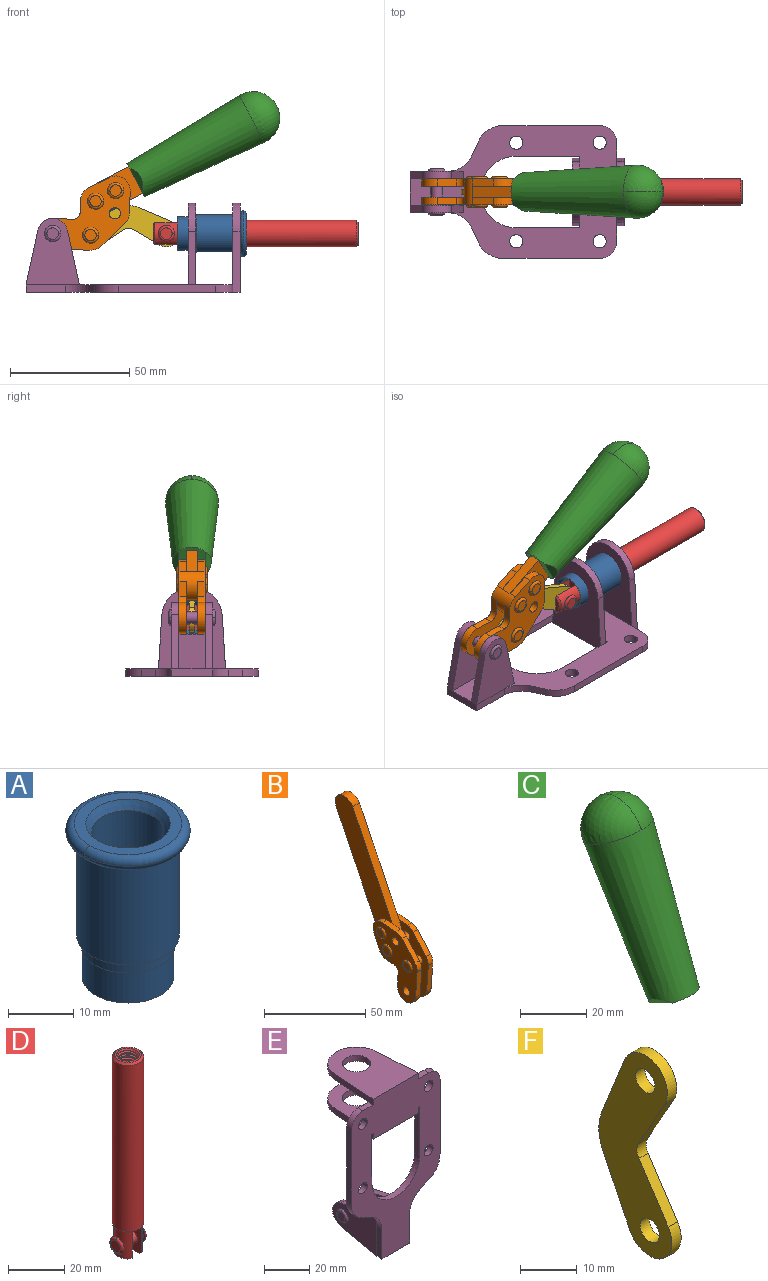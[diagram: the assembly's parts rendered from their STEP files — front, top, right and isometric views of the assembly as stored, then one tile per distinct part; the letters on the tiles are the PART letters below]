
ASSEMBLY  parts=6 mates=6
PART A: 15 faces, bbox 20.6x20.6x28.7 mm
  f0: torus R=8.26mm, axis (0,0,1), area 56.8mm2, adj f1,f10,f12
  f1: torus R=8.26mm, axis (0,0,1), area 56.8mm2, adj f0,f6,f13
  f2: cylinder r=5.59mm len=25.91mm, axis (0,0,1), area 909.6mm2, adj f3,f4
  f3: cone r=6.86mm half-angle=45deg, axis (0,0,-1), area 70.2mm2, adj f2,f14
  f4: cone r=6.47mm half-angle=30deg, axis (0,0,1), area 66.7mm2, adj f2,f13
  f5: cylinder r=7.04mm len=14.07mm, axis (0,0,1), area 252.6mm2, adj f11,f14
  f6: torus R=8.26mm, axis (0,0,1), area 56.8mm2, adj f1,f12,f13
  f7: cylinder r=7.16mm len=14.33mm, axis (0,0,1), area 91.5mm2, adj f9,f11
  f8: cylinder r=7.86mm len=18.42mm, axis (0,0,1), area 909.6mm2, adj f9,f10
  f9: plane 15.72x15.72mm, normal (0,0,-1), area 33mm2, adj f7,f8
  f10: plane 16.51x16.51mm, normal (0,0,-1), area 19.9mm2, adj f0,f8,f12
  f11: plane 14.33x14.33mm, normal (0,0,-1), area 5.7mm2, adj f5,f7
  f12: torus R=8.26mm, axis (0,0,1), area 56.8mm2, adj f0,f6,f10
  f13: plane 16.51x16.51mm, normal (0,0,1), area 82.7mm2, adj f1,f4,f6
  f14: plane 14.07x14.07mm, normal (0,0,-1), area 7.8mm2, adj f3,f5
PART B: 59 faces, bbox 12.9x60.2x99.6 mm
  f0: torus R=2.39mm, axis (-1,0,0), area 14.9mm2, adj f20,f43,f51
  f1: torus R=2.39mm, axis (-1,0,0), area 14.9mm2, adj f19,f42,f51
  f2: torus R=2.39mm, axis (-1,0,0), area 14.9mm2, adj f18,f35,f51
  f3: torus R=2.39mm, axis (-1,0,0), area 14.9mm2, adj f14,f17,f23
  f4: torus R=2.39mm, axis (-1,0,0), area 14.9mm2, adj f13,f16,f23
  f5: torus R=2.39mm, axis (-1,0,0), area 14.9mm2, adj f12,f15,f23
  f6: cylinder r=2.39mm len=4.78mm, axis (1,0,0), area 46.5mm2, adj f48,f50,f51
  f7: cylinder r=2.39mm len=4.78mm, axis (1,0,0), area 46.5mm2, adj f50,f51
  f8: cylinder r=6.35mm len=12.68mm, axis (1,0,0), area 61.8mm2, adj f38,f39,f50,f51
  f9: cylinder r=2.39mm len=4.78mm, axis (-1,0,0), area 70.5mm2, adj f46,f50
  f10: cylinder r=2.39mm len=4.78mm, axis (-1,0,0), area 46.5mm2, adj f23,f45,f46
  f11: cylinder r=2.39mm len=4.78mm, axis (-1,0,0), area 46.5mm2, adj f23,f46
  f12: plane 4.78x4.78mm, normal (1,0,0), area 17.9mm2, adj f5,f15
  f13: plane 4.78x4.78mm, normal (1,0,0), area 17.9mm2, adj f4,f16
  f14: plane 4.78x4.78mm, normal (1,0,0), area 17.9mm2, adj f3,f17
  f15: torus R=2.39mm, axis (-1,0,0), area 14.9mm2, adj f5,f12,f23
  f16: torus R=2.39mm, axis (-1,0,0), area 14.9mm2, adj f4,f13,f23
  f17: torus R=2.39mm, axis (-1,0,0), area 14.9mm2, adj f3,f14,f23
  f18: plane 4.78x4.78mm, normal (-1,0,0), area 17.9mm2, adj f2,f35
  f19: plane 4.78x4.78mm, normal (-1,0,0), area 17.9mm2, adj f1,f42
  f20: plane 4.78x4.78mm, normal (-1,0,0), area 17.9mm2, adj f0,f43
  f21: plane 2.26x0.2mm, normal (1,0,0), area 0.2mm2, adj f31,f44
  f22: plane 2.26x0.2mm, normal (-1,0,0), area 0.2mm2, adj f41,f44
  f23: plane 39.37x30.77mm, normal (1,0,0), area 565.5mm2, adj f3,f4,f5,f10,f11,f15,f16,f17
  f24: cylinder r=6.1mm len=4.15mm, axis (-1,0,0), area 14.7mm2, adj f23,f25,f32,f46
  f25: plane 10.25x9.01mm, normal (0,-0.75,0.66), area 42.3mm2, adj f23,f24,f26,f46
  f26: cylinder r=6.35mm len=4.64mm, axis (-1,0,0), area 15.6mm2, adj f23,f25,f27,f46
  f27: plane 15.84x3.1mm, normal (0,-1,-0.07), area 49.2mm2, adj f23,f26,f28,f46
  f28: cylinder r=6.35mm len=12.68mm, axis (-1,0,0), area 61.8mm2, adj f23,f27,f29,f46
  f29: plane 8.11x3.1mm, normal (0,1,0.07), area 25.2mm2, adj f23,f28,f30,f46
  f30: cylinder r=3.05mm len=3.25mm, axis (-1,0,0), area 14.8mm2, adj f23,f29,f31,f46
  f31: plane 5.99x3.1mm, normal (0,0.07,-1), area 18.6mm2, adj f21,f23,f30,f44,f46
  f32: plane 9.5x3.1mm, normal (0,-0.07,1), area 29.5mm2, adj f23,f24,f33,f46,f47
  f33: cylinder r=6.1mm len=8.63mm, axis (-1,0,0), area 39.1mm2, adj f23,f32,f34,f47
  f34: plane 8.65x3.96mm, normal (0,0.91,-0.42), area 29.5mm2, adj f23,f33,f44,f47
  f35: torus R=2.39mm, axis (-1,0,0), area 14.9mm2, adj f2,f18,f51
  f36: plane 10.25x9.01mm, normal (0,-0.75,0.66), area 42.3mm2, adj f37,f49,f50,f51
  f37: cylinder r=6.35mm len=4.64mm, axis (1,0,0), area 15.6mm2, adj f36,f38,f50,f51
  f38: plane 15.84x3.1mm, normal (0,-1,-0.07), area 49.2mm2, adj f8,f37,f50,f51
  f39: plane 8.11x3.1mm, normal (0,1,0.07), area 25.2mm2, adj f8,f40,f50,f51
  f40: cylinder r=3.05mm len=3.25mm, axis (1,0,0), area 14.8mm2, adj f39,f41,f50,f51
  f41: plane 5.99x3.1mm, normal (0,0.07,-1), area 18.6mm2, adj f22,f40,f44,f50,f51
  f42: torus R=2.39mm, axis (-1,0,0), area 14.9mm2, adj f1,f19,f51
  f43: torus R=2.39mm, axis (-1,0,0), area 14.9mm2, adj f0,f20,f51
  f44: cylinder r=6.35mm len=12.12mm, axis (-1,0,0), area 128.9mm2, adj f21,f22,f23,f31,f34,f41,f46,f47
  f45: plane 2.65x1.35mm, normal (1,0,0), area 1mm2, adj f10,f55
  f46: plane 39.08x20.42mm, normal (-1,0,0), area 412.5mm2, adj f9,f10,f11,f24,f25,f26,f27,f28
  f47: plane 77.62x39.82mm, normal (1,0,0), area 850mm2, adj f32,f33,f34,f44,f53,f54,f55
  f48: plane 2.65x1.35mm, normal (-1,0,0), area 1mm2, adj f6,f55
  f49: cylinder r=6.1mm len=4.15mm, axis (1,0,0), area 14.7mm2, adj f36,f50,f51,f56
  f50: plane 39.08x20.42mm, normal (1,0,0), area 412.5mm2, adj f6,f7,f8,f9,f36,f37,f38,f39
  f51: plane 39.37x30.77mm, normal (-1,0,0), area 565.5mm2, adj f0,f1,f2,f6,f7,f8,f35,f36
  f52: plane 8.65x3.96mm, normal (0,0.91,-0.42), area 29.5mm2, adj f44,f51,f57,f58
  f53: plane 68.49x33.4mm, normal (0,0.9,-0.44), area 358.1mm2, adj f44,f47,f54,f58
  f54: cylinder r=6.35mm len=12.06mm, axis (1,0,0), area 93.7mm2, adj f47,f53,f55,f58
  f55: plane 68.49x33.4mm, normal (0,-0.9,0.44), area 358.1mm2, adj f44,f45,f46,f47,f48,f50,f54,f58
  f56: plane 9.5x3.1mm, normal (0,-0.07,1), area 29.5mm2, adj f49,f50,f51,f57,f58
  f57: cylinder r=6.1mm len=8.63mm, axis (1,0,0), area 39.1mm2, adj f51,f52,f56,f58
  f58: plane 77.62x39.82mm, normal (-1,0,0), area 850mm2, adj f44,f52,f53,f54,f55,f56,f57
PART C: 11 faces, bbox 22.3x42.6x64.5 mm
  f0: sphere r=11.13mm, area 411.4mm2, adj f1,f8
  f1: cone r=11.11mm half-angle=3.3deg, axis (0,0.44,0.9), area 3251.8mm2, adj f0,f7,f8,f9,f10
  f2: cylinder r=6.16mm len=11.7mm, axis (1,0,0), area 89.5mm2, adj f3,f4,f5,f6
  f3: plane 60.23x36.75mm, normal (-1,0,0), area 763.6mm2, adj f2,f4,f6,f10
  f4: plane 51.37x25.05mm, normal (0,0.9,-0.44), area 264.2mm2, adj f2,f3,f5,f10
  f5: plane 60.23x36.75mm, normal (1,0,0), area 763.6mm2, adj f2,f4,f6,f10
  f6: plane 51.37x25.05mm, normal (0,-0.9,0.44), area 264.2mm2, adj f2,f3,f5,f10
  f7: plane 9.95x5.95mm, normal (0.71,-0.31,-0.64), area 25.8mm2, adj f1,f10
  f8: sphere r=11.13mm, area 411.4mm2, adj f0,f1
  f9: plane 9.95x5.95mm, normal (-0.71,-0.31,-0.64), area 25.8mm2, adj f1,f10
  f10: plane 14.27x11.38mm, normal (0,-0.44,-0.9), area 106.7mm2, adj f1,f3,f4,f5,f6,f7,f9
PART D: 48 faces, bbox 12.6x11.1x86.1 mm
  f0: torus R=2.41mm, axis (-1,0,0), area 15mm2, adj f30,f32,f34
  f1: torus R=2.41mm, axis (-1,0,0), area 15mm2, adj f29,f31,f33
  f2: cylinder r=5.54mm len=72.39mm, axis (0,0,1), area 2518.5mm2, adj f3,f4,f42,f43
  f3: cone r=5.54mm half-angle=45deg, axis (0,0,1), area 7.6mm2, adj f2,f5,f41
  f4: cone r=5.54mm half-angle=45deg, axis (0,0,-1), area 34.9mm2, adj f2,f39
  f5: cylinder r=5.08mm len=11.48mm, axis (0,0,1), area 108.3mm2, adj f3,f7,f8,f41
  f6: cylinder r=2.41mm len=4.83mm, axis (-1,0,0), area 71.2mm2, adj f40,f41
  f7: cylinder r=2.41mm len=4.83mm, axis (-1,0,0), area 7.6mm2, adj f5,f34
  f8: cone r=5.08mm half-angle=45deg, axis (0,0,1), area 10.6mm2, adj f5,f37,f41
  f9: cone r=3.98mm half-angle=45deg, axis (0,0,1), area 17.6mm2, adj f27,f39,f45,f46,f47
  f10: cylinder r=2.41mm len=4.83mm, axis (-1,0,0), area 7.6mm2, adj f33,f38
  f11: cylinder r=3.2mm len=6.4mm, axis (0,0,1), area 78.4mm2, adj f12,f28,f44,f45,f47
  f12: cylinder r=3.2mm len=6.4mm, axis (0,0,1), area 10.5mm2, adj f11,f13,f45,f47
  f13: cylinder r=3.2mm len=6.4mm, axis (0,0,1), area 10.5mm2, adj f12,f14,f45,f47
  f14: cylinder r=3.2mm len=6.4mm, axis (0,0,1), area 10.5mm2, adj f13,f15,f45,f47
  f15: cylinder r=3.2mm len=6.4mm, axis (0,0,1), area 10.5mm2, adj f14,f16,f45,f47
  f16: cylinder r=3.2mm len=6.4mm, axis (0,0,1), area 10.5mm2, adj f15,f17,f45,f47
  f17: cylinder r=3.2mm len=6.4mm, axis (0,0,1), area 10.5mm2, adj f16,f18,f45,f47
  f18: cylinder r=3.2mm len=6.4mm, axis (0,0,1), area 10.5mm2, adj f17,f19,f45,f47
  f19: cylinder r=3.2mm len=6.4mm, axis (0,0,1), area 10.5mm2, adj f18,f20,f45,f47
  f20: cylinder r=3.2mm len=6.4mm, axis (0,0,1), area 10.5mm2, adj f19,f21,f45,f47
  f21: cylinder r=3.2mm len=6.4mm, axis (0,0,1), area 10.5mm2, adj f20,f22,f45,f47
  f22: cylinder r=3.2mm len=6.4mm, axis (0,0,1), area 10.5mm2, adj f21,f23,f45,f47
  f23: cylinder r=3.2mm len=6.4mm, axis (0,0,1), area 10.5mm2, adj f22,f24,f45,f47
  f24: cylinder r=3.2mm len=6.4mm, axis (0,0,1), area 10.5mm2, adj f23,f25,f45,f47
  f25: cylinder r=3.2mm len=6.4mm, axis (0,0,1), area 10.5mm2, adj f24,f26,f45,f47
  f26: cylinder r=3.2mm len=6.4mm, axis (0,0,1), area 10.5mm2, adj f25,f27,f45,f47
  f27: cylinder r=3.2mm len=6.4mm, axis (0,0,1), area 7.4mm2, adj f9,f26,f45,f47
  f28: cone r=3.2mm half-angle=60deg, axis (0,0,1), area 37.2mm2, adj f11
  f29: plane 4.83x4.83mm, normal (-1,0,0), area 18.3mm2, adj f1,f31
  f30: plane 4.83x4.83mm, normal (1,0,0), area 18.3mm2, adj f0,f32
  f31: torus R=2.41mm, axis (-1,0,0), area 15mm2, adj f1,f29,f33
  f32: torus R=2.41mm, axis (-1,0,0), area 15mm2, adj f0,f30,f34
  f33: plane 6.83x6.83mm, normal (1,0,0), area 18.3mm2, adj f1,f10,f31
  f34: plane 6.83x6.83mm, normal (-1,0,0), area 18.3mm2, adj f0,f7,f32
  f35: cone r=5.08mm half-angle=45deg, axis (0,0,1), area 10.6mm2, adj f36,f38,f40
  f36: plane 7.25x1.97mm, normal (0,0,-1), area 10mm2, adj f35,f40
  f37: plane 7.25x1.97mm, normal (0,0,-1), area 10mm2, adj f8,f41
  f38: cylinder r=5.08mm len=11.48mm, axis (0,0,1), area 108.3mm2, adj f10,f35,f40,f42
  f39: plane 9.55x9.55mm, normal (0,0,1), area 22mm2, adj f4,f9
  f40: plane 12.76x10.09mm, normal (1,0,0), area 95.7mm2, adj f6,f35,f36,f38,f42,f43
  f41: plane 12.76x10.09mm, normal (-1,0,0), area 95.7mm2, adj f3,f5,f6,f8,f37,f43
  f42: cone r=5.54mm half-angle=45deg, axis (0,0,1), area 7.6mm2, adj f2,f38,f40
  f43: plane 11.07x4.7mm, normal (0,0,-1), area 50.4mm2, adj f2,f40,f41
  f44: plane 0.89x0.62mm, normal (-1,0,0), area 0.3mm2, adj f11,f45,f46,f47
  f45: bspline ~24.8x7.63mm, area 266.6mm2, adj f9,f11,f12,f13,f14,f15,f16,f17
  f46: bspline ~24.87x7.63mm, area 73.6mm2, adj f9,f44,f45,f47
  f47: bspline ~24.98x7.63mm, area 272.5mm2, adj f9,f11,f12,f13,f14,f15,f16,f17
PART E: 55 faces, bbox 55.7x37.4x89.8 mm
  f0: torus R=2.41mm, axis (-1,0,0), area 15mm2, adj f11,f15,f25
  f1: torus R=2.41mm, axis (-1,0,0), area 15mm2, adj f10,f12,f22
  f2: cylinder r=2.78mm len=5.56mm, axis (0,-1,0), area 54.2mm2, adj f30,f54
  f3: cylinder r=14.99mm len=29.97mm, axis (0,-1,0), area 145.9mm2, adj f30,f49,f53,f54
  f4: cylinder r=2.78mm len=5.56mm, axis (0,-1,0), area 54.2mm2, adj f30,f54
  f5: cylinder r=2.78mm len=5.56mm, axis (0,-1,0), area 54.2mm2, adj f30,f54
  f6: cylinder r=2.78mm len=5.56mm, axis (0,-1,0), area 54.2mm2, adj f30,f54
  f7: cylinder r=6.35mm len=12.7mm, axis (0,0,1), area 123.6mm2, adj f27,f51
  f8: cylinder r=6.35mm len=12.7mm, axis (0,0,-1), area 124.7mm2, adj f21,f35
  f9: cylinder r=2.41mm len=11.18mm, axis (-1,0,0), area 169.4mm2, adj f16,f19
  f10: plane 4.83x4.83mm, normal (1,0,0), area 18.3mm2, adj f1,f12
  f11: plane 4.83x4.83mm, normal (-1,0,0), area 18.3mm2, adj f0,f15
  f12: torus R=2.41mm, axis (-1,0,0), area 15mm2, adj f1,f10,f22
  f13: cylinder r=6.35mm len=12.41mm, axis (1,0,0), area 53.4mm2, adj f18,f19,f22,f23
  f14: cylinder r=6.35mm len=12.41mm, axis (-1,0,0), area 53.4mm2, adj f16,f17,f24,f25
  f15: torus R=2.41mm, axis (-1,0,0), area 15mm2, adj f0,f11,f25
  f16: plane 27.86x22.35mm, normal (1,0,0), area 425.4mm2, adj f9,f14,f17,f24,f30
  f17: plane 22.86x4.97mm, normal (0,0.21,0.98), area 72.5mm2, adj f14,f16,f25,f30
  f18: plane 22.86x4.97mm, normal (0,0.21,0.98), area 72.5mm2, adj f13,f19,f22,f30
  f19: plane 27.86x22.35mm, normal (-1,0,0), area 425.4mm2, adj f9,f13,f18,f23,f30
  f20: cylinder r=12.7mm len=25.35mm, axis (0,0,-1), area 119.8mm2, adj f21,f34,f35,f36
  f21: plane 34.21x28.07mm, normal (0,0,-1), area 702.4mm2, adj f8,f20,f30,f34,f36
  f22: plane 27.96x22.45mm, normal (1,0,0), area 407.2mm2, adj f1,f12,f13,f18,f23,f30,f42,f43
  f23: plane 22.86x4.97mm, normal (0,0.21,-0.98), area 72.5mm2, adj f13,f19,f22,f44
  f24: plane 22.86x4.97mm, normal (0,0.21,-0.98), area 72.5mm2, adj f14,f16,f25,f44
  f25: plane 27.86x22.35mm, normal (-1,0,0), area 407.1mm2, adj f0,f14,f15,f17,f24,f30,f45,f46
  f26: plane 3.1x0.95mm, normal (0,0,-1), area 2.7mm2, adj f30,f49,f50,f54
  f27: plane 34.21x28.07mm, normal (0,0,1), area 702.4mm2, adj f7,f28,f30,f50,f52
  f28: cylinder r=12.7mm len=25.35mm, axis (0,0,1), area 118.8mm2, adj f27,f50,f51,f52
  f29: plane 3.1x0.95mm, normal (0,0,-1), area 2.7mm2, adj f30,f52,f53,f54
  f30: plane 86.54x55.63mm, normal (0,1,0), area 2362.9mm2, adj f2,f3,f4,f5,f6,f16,f17,f18
  f31: plane 40.56x3.1mm, normal (-1,0,0), area 125.7mm2, adj f30,f32,f48,f54
  f32: cylinder r=7.11mm len=7.11mm, axis (0,-1,0), area 34.6mm2, adj f30,f31,f33,f54
  f33: plane 6.67x3.1mm, normal (0,0,1), area 20.4mm2, adj f30,f32,f34,f54
  f34: plane 25.39x3.13mm, normal (-1,0.06,0), area 79.5mm2, adj f20,f21,f33,f35,f54
  f35: plane 37.31x28.45mm, normal (0,0,1), area 789.9mm2, adj f8,f20,f34,f36,f54
  f36: plane 25.39x3.13mm, normal (1,0.06,0), area 79.5mm2, adj f20,f21,f35,f37,f54
  f37: plane 6.67x3.1mm, normal (0,0,1), area 20.4mm2, adj f30,f36,f38,f54
  f38: cylinder r=7.11mm len=7.11mm, axis (0,-1,0), area 34.6mm2, adj f30,f37,f39,f54
  f39: plane 40.56x3.1mm, normal (1,0,0), area 125.7mm2, adj f30,f38,f40,f54
  f40: cylinder r=11.18mm len=10.16mm, axis (0,-1,0), area 39.5mm2, adj f30,f39,f41,f54
  f41: plane 6.09x3.1mm, normal (0.42,0,-0.91), area 20.8mm2, adj f30,f40,f42,f54
  f42: cylinder r=11.18mm len=9.41mm, axis (0,-1,0), area 37.2mm2, adj f22,f30,f41,f43,f54
  f43: plane 16.5x3.1mm, normal (1,0,0), area 51.1mm2, adj f22,f42,f44,f54
  f44: plane 17.37x3.1mm, normal (0,0,-1), area 53.8mm2, adj f23,f24,f30,f43,f45,f54
  f45: plane 16.5x3.1mm, normal (-1,0,0), area 51.1mm2, adj f25,f44,f46,f54
  f46: cylinder r=11.18mm len=9.41mm, axis (0,-1,0), area 37.2mm2, adj f25,f30,f45,f47,f54
  f47: plane 6.09x3.1mm, normal (-0.42,0,-0.91), area 20.8mm2, adj f30,f46,f48,f54
  f48: cylinder r=11.18mm len=10.16mm, axis (0,-1,0), area 39.5mm2, adj f30,f31,f47,f54
  f49: plane 26.54x3.1mm, normal (-1,0,0), area 82.3mm2, adj f3,f26,f30,f54
  f50: plane 25.39x3.1mm, normal (1,0.06,0), area 78.8mm2, adj f26,f27,f28,f51,f54
  f51: plane 37.31x28.45mm, normal (0,0,-1), area 789.9mm2, adj f7,f28,f50,f52,f54
  f52: plane 25.39x3.1mm, normal (-1,0.06,0), area 78.8mm2, adj f27,f28,f29,f51,f54
  f53: plane 26.54x3.1mm, normal (1,0,0), area 82.3mm2, adj f3,f29,f30,f54
  f54: plane 89.66x55.63mm, normal (0,-1,0), area 2678.5mm2, adj f2,f3,f4,f5,f6,f26,f29,f31
PART F: 12 faces, bbox 2.3x18.2x42.8 mm
  f0: cylinder r=2.4mm len=4.8mm, axis (1,0,0), area 34.9mm2, adj f4,f11
  f1: cylinder r=10.41mm len=8.47mm, axis (1,0,0), area 20.2mm2, adj f4,f9,f10,f11
  f2: cylinder r=3.05mm len=3.16mm, axis (1,0,0), area 7.7mm2, adj f4,f6,f7,f11
  f3: cylinder r=2.4mm len=4.8mm, axis (1,0,0), area 34.9mm2, adj f4,f11
  f4: plane 42.81x18.23mm, normal (-1,0,0), area 414.1mm2, adj f0,f1,f2,f3,f5,f6,f7,f8
  f5: cylinder r=5.54mm len=10.67mm, axis (1,0,0), area 41.8mm2, adj f4,f6,f10,f11
  f6: plane 11.66x6.53mm, normal (0,-0.87,-0.49), area 30.9mm2, adj f2,f4,f5,f11
  f7: plane 11.17x7.33mm, normal (0,-0.84,0.55), area 30.9mm2, adj f2,f4,f8,f11
  f8: cylinder r=5.54mm len=10.51mm, axis (1,0,0), area 41.8mm2, adj f4,f7,f9,f11
  f9: plane 13.67x6.67mm, normal (0,0.9,-0.44), area 35.1mm2, adj f1,f4,f8,f11
  f10: plane 14.1x5.7mm, normal (0,0.93,0.37), area 35.1mm2, adj f1,f4,f5,f11
  f11: plane 42.81x18.23mm, normal (1,0,0), area 414.1mm2, adj f0,f1,f2,f3,f5,f6,f7,f8
PLACE A rot(axis=(0.71,0,0.71),180deg) t=(-33.5,32.07,24.76)mm
PLACE B rot(axis=(0.57,0.57,0.59),119deg) t=(-32.75,7.46,1.15)mm
PLACE C rot(axis=(0.57,0.57,0.59),119deg) t=(-32.75,7.46,1.15)mm
PLACE D rot(axis=(0.58,0.58,0.58),120deg) t=(-33.46,7.46,0.15)mm
PLACE E rot(axis=(0.58,0.58,0.58),120deg) t=(-33.5,7.46,0.15)mm fixed
PLACE F rot(axis=(0.59,-0.59,-0.56),121.8deg) t=(-32.94,7.46,0.41)mm
MATE revolute F.f3 <-> D.f6  axis (0,-1,0) through (-17.98,7.46,24.76)mm
MATE revolute B.f7 <-> E.f0  axis (0,-1,0) through (-65.59,7.46,24.76)mm
MATE fastened C.f2 <-> B.f54  axis (0,1,0) through (19.8,7.46,73.85)mm
MATE revolute F.f5 <-> B.f4  axis (0,-1,0) through (-49.73,7.46,24.14)mm
MATE fastened A.f0 <-> E.f7  axis (-1,0,0) through (12.89,7.46,24.76)mm
MATE slider D.f2 <-> A.f2  axis (1,0,0) through (25.32,7.46,24.76)mm
